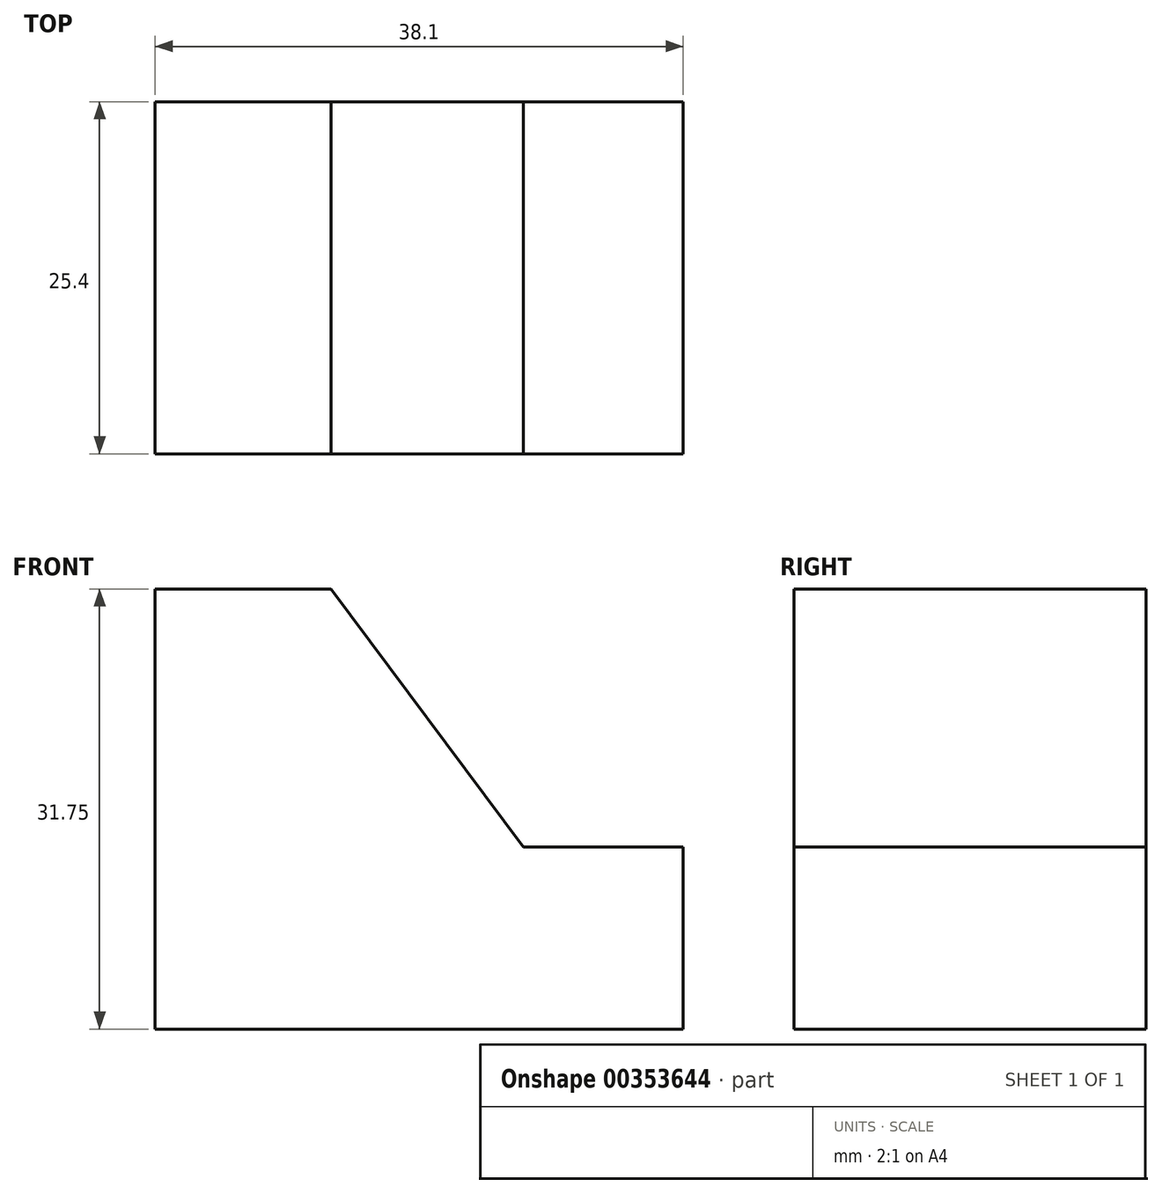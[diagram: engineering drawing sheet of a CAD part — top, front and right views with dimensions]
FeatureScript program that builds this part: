
annotation { "Feature Type Name" : "Feature", "Feature Type Description" : "" }
export const myFeature = defineFeature(function(context is Context, id is Id, definition is map)
    precondition{}
    {
        {
            var Q0;
            Q0=qCreatedBy(makeId("Front.planeOp"),FACE);
            var sketch = newSketch(context, id + "F0", { "sketchPlane" : qUnion([Q0])});
            skLineSegment(sketch, "E0", {"start": v(-50.8, 31.75) * mm, "end": v(-50.8, 0) * mm});
            skLineSegment(sketch, "E1", {"start": v(-50.8, 31.75) * mm, "end": v(-38.1, 31.75) * mm});
            skLineSegment(sketch, "E2", {"start": v(-38.1, 31.75) * mm, "end": v(-24.24, 13.13) * mm});
            skLineSegment(sketch, "E3", {"start": v(-25.4, 13.13) * mm, "end": v(-12.7, 13.13) * mm});
            skLineSegment(sketch, "E4", {"start": v(-12.7, 13.13) * mm, "end": v(-12.7, 0) * mm});
            skLineSegment(sketch, "E5", {"start": v(-50.8, 0) * mm, "end": v(-12.7, 0) * mm});
            skSolve(sketch);
        }
        {
            var Q0;
            Q0=makeQuery(id+"F0.imprint","IMPRINT",FACE,{"disambiguationData":[TD([[makeQuery(id+"F0.imprint","IMPRINT",EDGE,{"derivedFrom":sQuery(id+"F0.wireOp",EDGE,"E0")}),1.0]])]});
            extrude(context, id + "F1", {"entities" : qUnion([Q0]), "depth" : 25.4 * mm});
        }
    });
